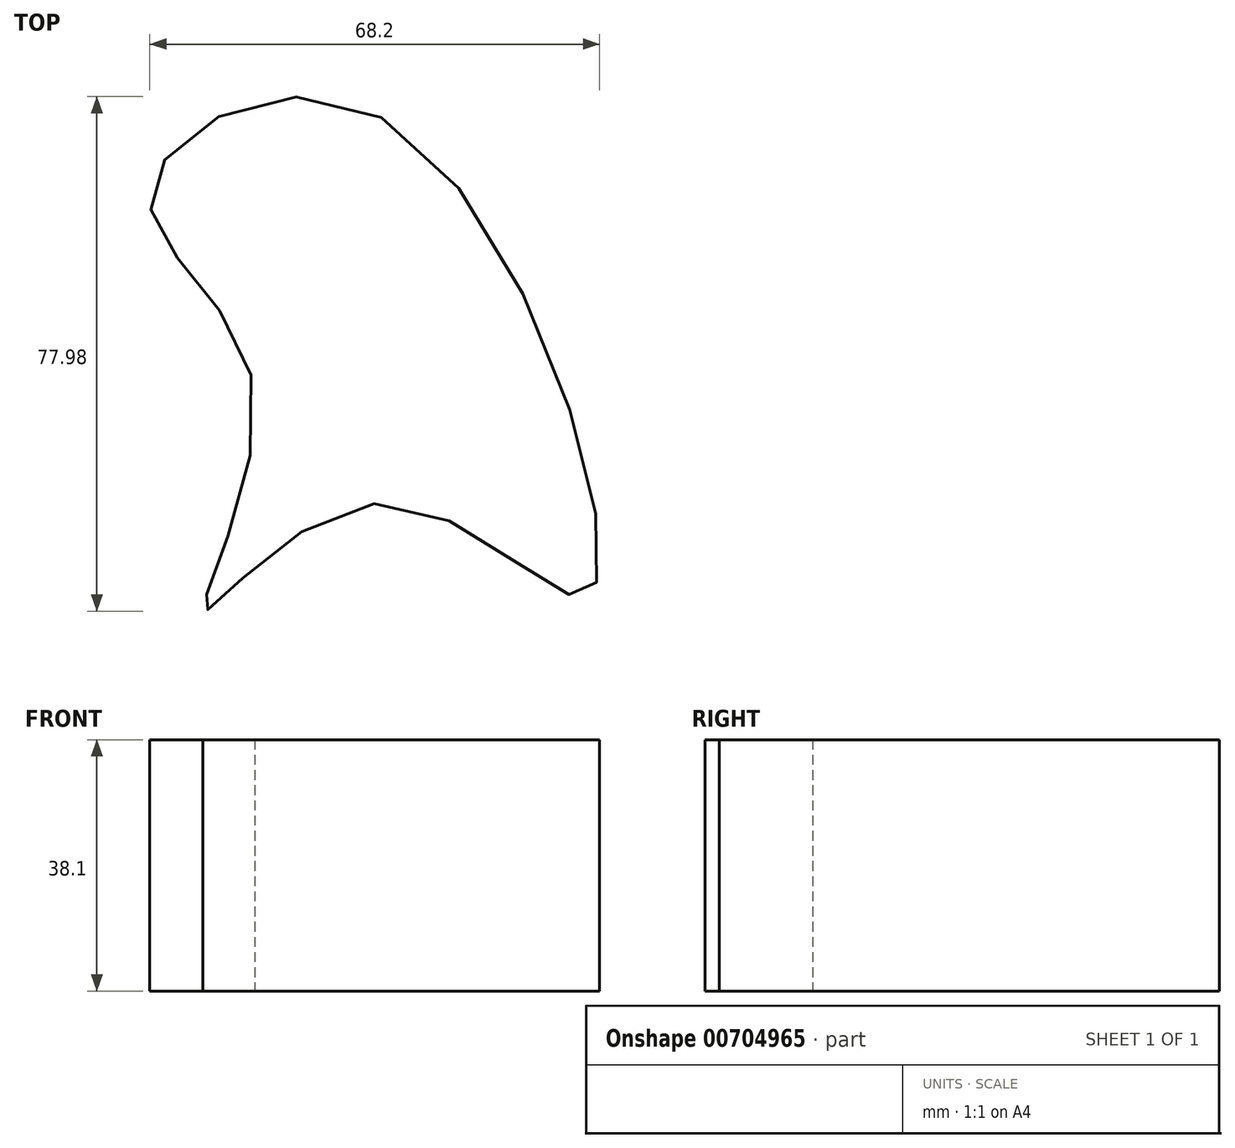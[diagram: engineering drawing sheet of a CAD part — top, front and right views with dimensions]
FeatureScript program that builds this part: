
annotation { "Feature Type Name" : "Feature", "Feature Type Description" : "" }
export const myFeature = defineFeature(function(context is Context, id is Id, definition is map)
    precondition{}
    {
        {
            var Q0;
            Q0=qCreatedBy(makeId("Top.planeOp"),FACE);
            var sketch = newSketch(context, id + "F0", { "sketchPlane" : qUnion([Q0])});
            skFitSpline(sketch, "E0", {"points": [v(0, 40.57) * mm, v(-35.01, 29.09) * mm, v(-19.45, 0) * mm, v(-26.86, -34.27) * mm, v(0, -17.97) * mm, v(31.68, -31.68) * mm, v(0, 40.57) * mm]});
            skSolve(sketch);
        }
        {
            var Q0;
            Q0=makeQuery(id+"F0.imprint","IMPRINT",FACE,{"disambiguationData":[TD([[makeQuery(id+"F0.imprint","IMPRINT",EDGE,{"derivedFrom":sQuery(id+"F0.wireOp",EDGE,"E0")}),1.0]])]});
            extrude(context, id + "F1", {"entities" : qUnion([Q0]), "depth" : 38.1 * mm, "offsetDistance" : 25.4 * mm});
        }
    });
